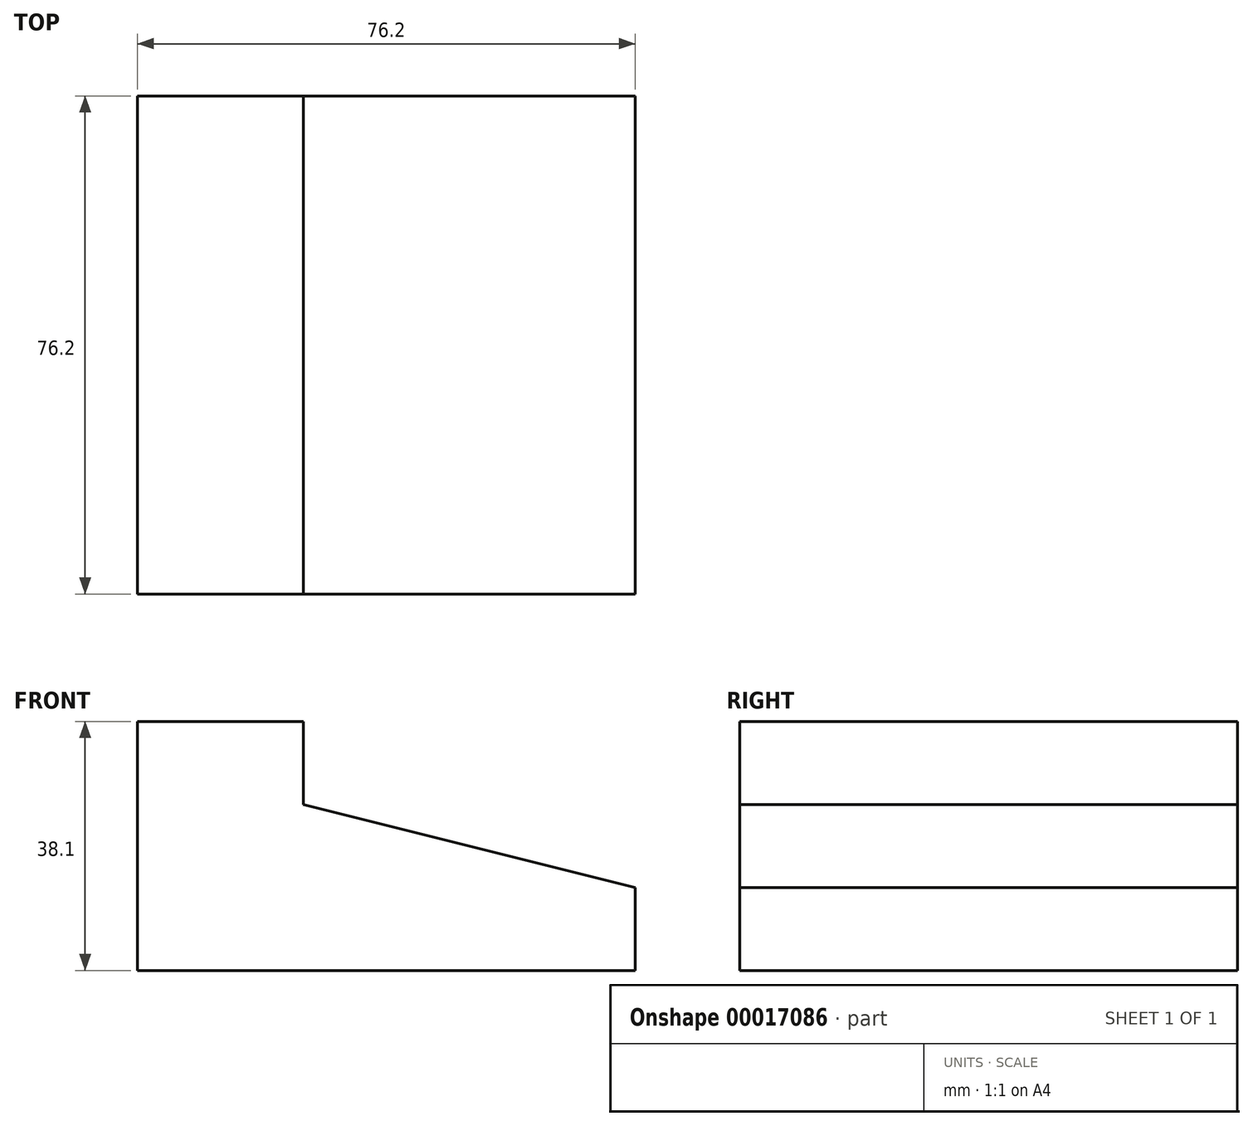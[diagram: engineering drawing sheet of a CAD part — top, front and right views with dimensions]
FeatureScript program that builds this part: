
annotation { "Feature Type Name" : "Feature", "Feature Type Description" : "" }
export const myFeature = defineFeature(function(context is Context, id is Id, definition is map)
    precondition{}
    {
        {
            var Q0;
            Q0=qCreatedBy(makeId("Front.planeOp"),FACE);
            var sketch = newSketch(context, id + "F0", { "sketchPlane" : qUnion([Q0])});
            skLineSegment(sketch, "E0", {"start": v(-64.79, 17.65) * mm, "end": v(-64.79, -20.45) * mm});
            skLineSegment(sketch, "E1", {"start": v(-64.79, -20.45) * mm, "end": v(11.41, -20.45) * mm});
            skLineSegment(sketch, "E2", {"start": v(11.41, -20.45) * mm, "end": v(11.41, -7.75) * mm});
            skLineSegment(sketch, "E3", {"start": v(-64.79, 17.65) * mm, "end": v(-39.39, 17.65) * mm});
            skLineSegment(sketch, "E4", {"start": v(-39.39, 17.65) * mm, "end": v(-39.39, 4.95) * mm});
            skLineSegment(sketch, "E5", {"start": v(-39.39, 4.95) * mm, "end": v(11.41, -7.75) * mm});
            skSolve(sketch);
        }
        {
            var Q0;
            Q0 = qSketchRegion(id + "F0", true);
            var Q1;
            Q1=makeQuery(id+"F0.imprint","IMPRINT",FACE,{"disambiguationData":[TD([[makeQuery(id+"F0.imprint","IMPRINT",EDGE,{"derivedFrom":sQuery(id+"F0.wireOp",EDGE,"E0")}),1.0]])]});
            extrude(context, id + "F1", {"entities" : qUnion([Q0, Q1]), "depth" : 76.2 * mm});
        }
    });
